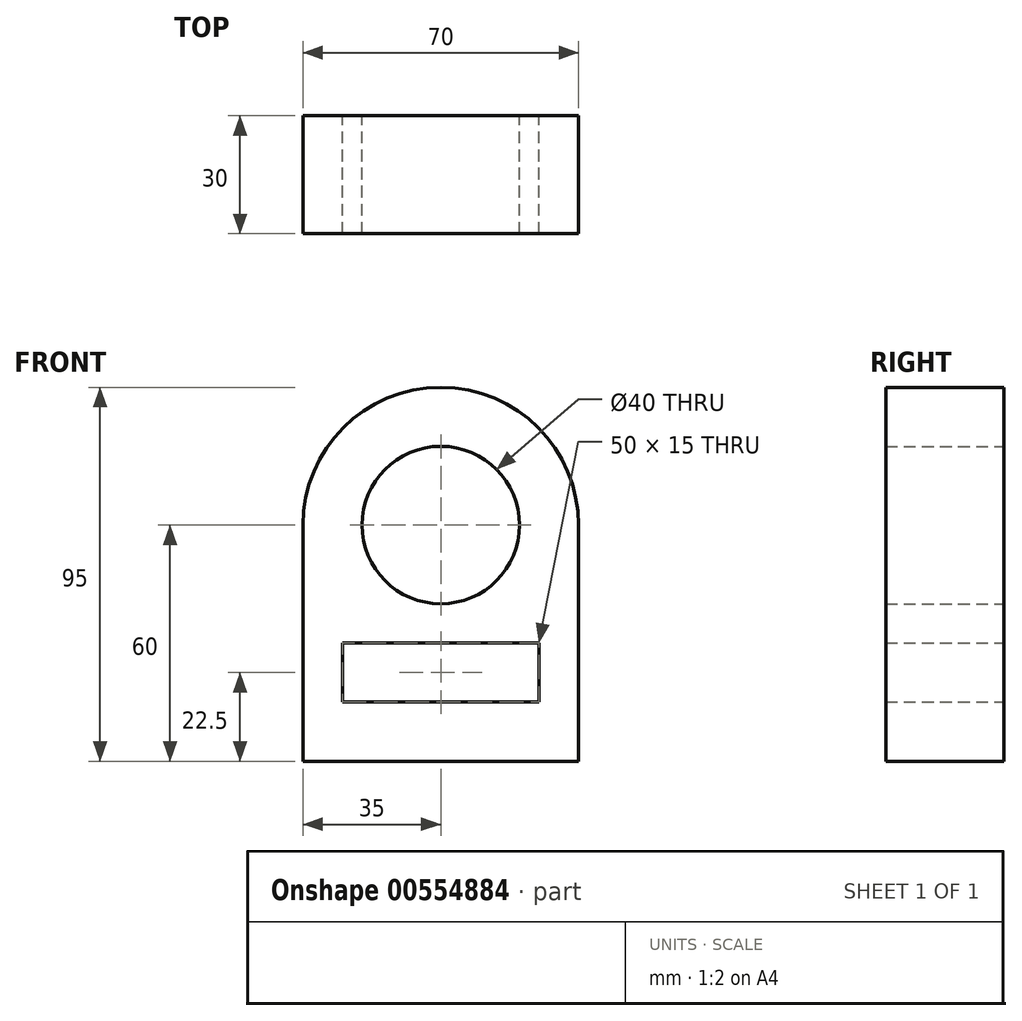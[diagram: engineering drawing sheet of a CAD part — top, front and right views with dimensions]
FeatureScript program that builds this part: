
annotation { "Feature Type Name" : "Feature", "Feature Type Description" : "" }
export const myFeature = defineFeature(function(context is Context, id is Id, definition is map)
    precondition{}
    {
        {
            var Q0;
            Q0=qCreatedBy(makeId("Front.planeOp"),FACE);
            var sketch = newSketch(context, id + "F0", { "sketchPlane" : qUnion([Q0])});
            skLineSegment(sketch, "E0", {"start": v(-48.8, -60) * mm, "end": v(21.2, -60) * mm});
            skLineSegment(sketch, "E1", {"start": v(-48.8, -60) * mm, "end": v(-48.8, 0) * mm});
            skLineSegment(sketch, "E2", {"start": v(21.2, -60) * mm, "end": v(21.2, 0) * mm});
            skArc(sketch, "E3", {"start": v(21.2, 0) * mm, "mid": v(-13.8, 35) * mm, "end": v(-48.8, 0) * mm});
            skCircle(sketch, "E4", {"center": v(-13.8, 0) * mm, "radius": 20 * mm});
            skLineSegment(sketch, "E5.bottom", {"start": v(-38.8, -30) * mm, "end": v(11.2, -30) * mm});
            skLineSegment(sketch, "E5.top", {"start": v(-38.8, -45) * mm, "end": v(11.2, -45) * mm});
            skLineSegment(sketch, "E5.left", {"start": v(-38.8, -30) * mm, "end": v(-38.8, -45) * mm});
            skLineSegment(sketch, "E5.right", {"start": v(11.2, -30) * mm, "end": v(11.2, -45) * mm});
            skSolve(sketch);
        }
        {
            var Q0;
            Q0 = qSketchRegion(id + "F0", true);
            extrude(context, id + "F1", {"entities" : qUnion([Q0]), "depth" : 30 * mm, "offsetDistance" : 25 * mm});
        }
    });
